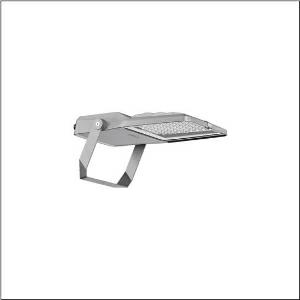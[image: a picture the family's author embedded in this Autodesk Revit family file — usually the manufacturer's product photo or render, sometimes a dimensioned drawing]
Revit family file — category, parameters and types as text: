
# Revit family: floodlight_fl_21_iq_mini___pl43_5xa7772b5a1a_c178
name_source: partatom
category: Lighting Fixtures
units: mm (PartAtom-declared; Revit-internal decimal feet)

## family parameters
Cut with Voids When Loaded = No
Host = Face
Light Source = No
Part Type = Normal
Room Calculation Point = No
Round Connector Dimension = Use Diameter
Shared = No

## types (1)
- --- (1 x LED, 5970 lm, 45.5 W, 4000K)
    Apparent Load = 46 VA
    CIE Flux Codes = 27 78 99 100 100
    Color Rendering = 80
    Color Temperature = 4000K
    Default Elevation = 1800 mm
    Description = Floodlight FL 21 iQ mini, floodlight, primary light control with lens, of PMMA, primary optical cover: protective disc, of toughened safety glass, transparent, light distribution: PL43, light emission: direct distribution, installation type: surface-mounted, LED, High Power LED, rated luminous flux: 5.970lm, luminous efficacy: 131lm/W, light colour: 840, colour temperature: 4000K, control gear: iQ Street-Remote/DALI, control: Street-Remote, Auto-Match, Temp-Guard, Night-Set, Smart-Wire, Desk-Remote (wireless, voltage-free reading and setting of iQ features in the workshop via application-optimized NFC function/RFID function), optimised constant luminous flux control (CLO 2.0), with terminal, 6-pole, mains connection: 220..240V, AC, 50/60Hz, start of lifetime: 46W, end of service life: 48W, reduction: 22W, luminaire housing, of diecast aluminium, powder-coated, Siteco® metallic grey (DB 702S), corrosivity category C5 mid according to DIN EN ISO 12944, suitable for swimming pools, chlorine-resistant, sealing non-destructively replaceable, mounting bracket, of steel, galvanised, powder-coated, Siteco® metallic grey (DB 702S), protection rating (complete): IP66, insulation class (complete): insulation class II (safety insulation), certification: CE, ENEC, VDE, protection symbol: D, impact resistance: IK08, permissible operating ambient temperature: -40..+40°C, permissible operating ambient temperature for outdoor applications: -40..+50°C, standard: DIN EN 12944, LABS conformity tested according to VDMA 24364:2018-05, packaging unit: 1 piece

Light Distribution: PL43
    Height = 70 mm
    Lamp = 1 x LED
    Lamp Light Flux = 5970 lm
    Lamp Power = 45.5 W
    Lamp count = 1
    Length = 485 mm
    Luminous efficacy = 131 lm/W
    Manufacturer = Siteco
    ModVariant = No
    Model = 5XA7772B5A1A
    Number of Poles = 1
    OnlyDefault = Yes
    Power Factor = 1
    Product Name = Floodlight FL 21 iQ mini | PL43
    Product group = floodlight | pylon annexe
    ProductGroupID = 6200
    Protection Class = Protection class II
    Protection Degree = IP 66
    RLX_Detail_Level = 1
    RLX_Emergency_Light_Flux = 0 lm
    RLX_Emergency_Type = 0
    RLX_Emergency_Type_DB = No
    RlxData = <blob elided: 96197 chars, md5=1c209a55>
    Socket = socket
    Standby Power = 0 W
    System Light Flux = 5970 lm
    System Power = 46 W
    Type Comments = factory setting: luminous flux: 100 % | dim-lin: 254 | 463 mA
    Type Image = l_1006845.jpg
    URL = http://relux.com
    VarID = @adj_162646
    Voltage = 0 V
    Weight = 0.00 kg
    Width = 337 mm

## geometry (parser evidence)
native form markers: Blend x4, Sweep x11
no freeform markers — native parametric forms only
